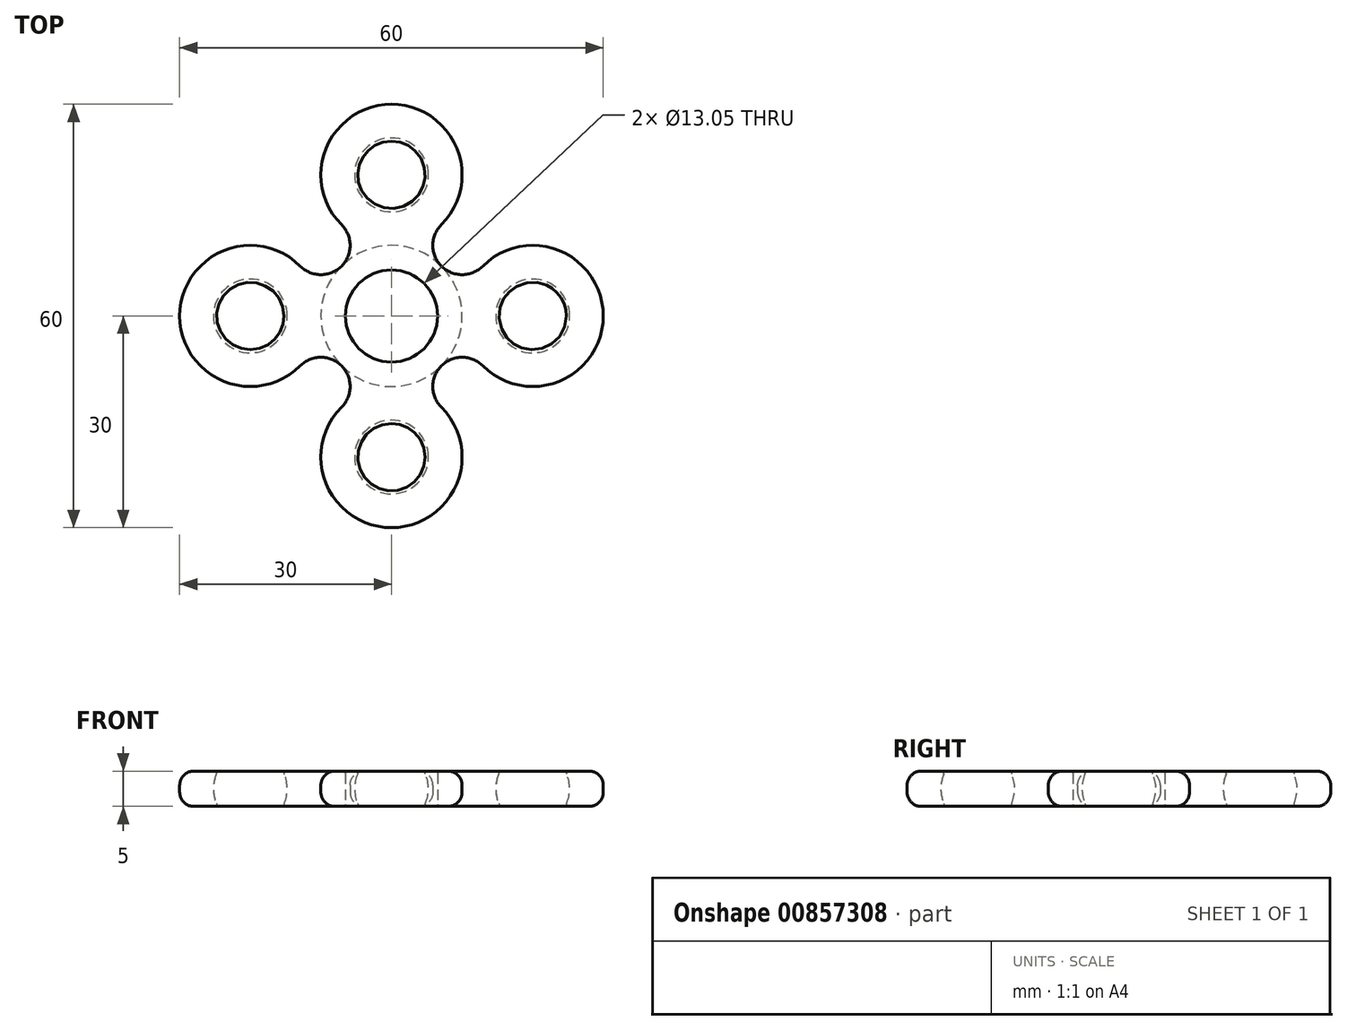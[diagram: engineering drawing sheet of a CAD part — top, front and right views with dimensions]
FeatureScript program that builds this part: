
annotation { "Feature Type Name" : "Feature", "Feature Type Description" : "" }
export const myFeature = defineFeature(function(context is Context, id is Id, definition is map)
    precondition{}
    {
        {
            var Q0;
            Q0=qCreatedBy(makeId("Top.planeOp"),FACE);
            var sketch = newSketch(context, id + "F0", { "sketchPlane" : qUnion([Q0])});
            skArc(sketch, "E0", {"start": v(-7.07, -7.07) * mm, "mid": v(0, -10) * mm, "end": v(7.07, -7.07) * mm});
            skArc(sketch, "E1", {"start": v(12.93, -7.07) * mm, "mid": v(30, 0) * mm, "end": v(12.93, 7.07) * mm});
            skArc(sketch, "E2", {"start": v(-12.93, 7.07) * mm, "mid": v(-30, 0) * mm, "end": v(-12.93, -7.07) * mm});
            skArc(sketch, "E3", {"start": v(7.07, 7.07) * mm, "mid": v(10, 5.86) * mm, "end": v(12.93, 7.07) * mm});
            skArc(sketch, "E4", {"start": v(-12.93, 7.07) * mm, "mid": v(-10, 5.86) * mm, "end": v(-7.07, 7.07) * mm});
            skArc(sketch, "E5.trimOffspring", {"start": v(7.07, 7.07) * mm, "mid": v(0, 10) * mm, "end": v(-7.07, 7.07) * mm});
            skArc(sketch, "E6", {"start": v(-7.07, -7.07) * mm, "mid": v(-10, -5.86) * mm, "end": v(-12.93, -7.07) * mm});
            skArc(sketch, "E7", {"start": v(12.93, -7.07) * mm, "mid": v(10, -5.86) * mm, "end": v(7.07, -7.07) * mm});
            skCircle(sketch, "E8", {"center": v(0, 0) * mm, "radius": 6.53 * mm});
            skSolve(sketch);
        }
        {
            var Q0;
            Q0=makeQuery(id+"F0.imprint","IMPRINT",FACE,{"disambiguationData":[TD([[makeQuery(id+"F0.imprint","IMPRINT",EDGE,{"derivedFrom":sQuery(id+"F0.wireOp",EDGE,"E0")}),1.0]])]});
            extrude(context, id + "F1", {"entities" : qUnion([Q0]), "depth" : 2.5 * mm, "offsetDistance" : 25 * mm});
        }
        {
            var Q0;
            Q0=makeQuery(id+"F1.opExtrude","CAP_FACE",FACE,{"disambiguationData":[OSD([sQuery(id+"F0.wireOp",EDGE,"E0"),sQuery(id+"F0.wireOp",EDGE,"E1"),sQuery(id+"F0.wireOp",EDGE,"E2"),sQuery(id+"F0.wireOp",EDGE,"E3"),sQuery(id+"F0.wireOp",EDGE,"E4"),sQuery(id+"F0.wireOp",EDGE,"E5.trimOffspring"),sQuery(id+"F0.wireOp",EDGE,"E6"),sQuery(id+"F0.wireOp",EDGE,"E7"),sQuery(id+"F0.wireOp",EDGE,"E8")])],"isStart":true});
            extrude(context, id + "F2", {"entities" : qUnion([Q0]), "operationType" : NewBodyOperationType.ADD, "depth" : 2.5 * mm, "offsetDistance" : 25 * mm});
        }
        {
            var Q0;
            Q0=qCreatedBy(makeId("Front.planeOp"),FACE);
            var sketch = newSketch(context, id + "F3", { "sketchPlane" : qUnion([Q0])});
            skArc(sketch, "E9", {"start": v(-20, 5.23) * mm, "mid": v(-25.23, 0) * mm, "end": v(-20, -5.23) * mm});
            skLineSegment(sketch, "E10", {"start": v(-20, 5.23) * mm, "end": v(-20, -5.23) * mm});
            skSolve(sketch);
        }
        {
            var Q0;
            Q0=qSketchRegion(id+"F3",true);
            var Q1;
            Q1=sQuery(id+"F3.wireOp",EDGE,"E10");
            revolve(context, id + "F4", {"operationType" : NewBodyOperationType.REMOVE, "entities" : qUnion([Q0]), "axis" : qUnion([Q1]), "revolveType" : RevolveType.FULL, "oppositeDirection" : true, "surfaceOperationType" : NewSurfaceOperationType.NEW});
        }
        {
            var Q0;
            Q0=qCreatedBy(makeId("Front.planeOp"),FACE);
            var sketch = newSketch(context, id + "F5", { "sketchPlane" : qUnion([Q0])});
            skArc(sketch, "E11", {"start": v(20, -5.23) * mm, "mid": v(25.23, 0) * mm, "end": v(20, 5.23) * mm});
            skLineSegment(sketch, "E12", {"start": v(20, 5.23) * mm, "end": v(20, -5.23) * mm});
            skPoint(sketch, "E13.orphan", {"position": v(20, 9.13) * mm});
            skSolve(sketch);
        }
        {
            var Q0;
            Q0=makeQuery(id+"F5.imprint","IMPRINT",FACE,{"disambiguationData":[TD([[makeQuery(id+"F5.imprint","IMPRINT",EDGE,{"derivedFrom":sQuery(id+"F5.wireOp",EDGE,"E11")}),1.0]])]});
            var Q1;
            Q1=sQuery(id+"F5.wireOp",EDGE,"E12");
            revolve(context, id + "F6", {"operationType" : NewBodyOperationType.REMOVE, "entities" : qUnion([Q0]), "axis" : qUnion([Q1]), "revolveType" : RevolveType.FULL, "oppositeDirection" : true});
        }
        {
            var Q0;
            Q0=makeQuery(id+"F2.opExtrude","CAP_EDGE",EDGE,{"disambiguationData":[OSD([sQuery(id+"F0.wireOp",EDGE,"E6")])],"isStart":false});
            var Q1;
            Q1=makeQuery(id+"F1.opExtrude","CAP_EDGE",EDGE,{"disambiguationData":[OSD([sQuery(id+"F0.wireOp",EDGE,"E0")])],"isStart":false});
            fillet(context, id + "F7", {"entities" : qUnion([Q0, Q1]), "radius" : 2 * mm, "tangentPropagation" : true, "allowEdgeOverflow" : false});
        }
        {
            var Q0;
            Q0=makeQuery(id+"F6.boolean.opBoolean","COPY",FACE,{"derivedFrom":makeQuery(id+"F6.opRevolve","SWEPT_FACE",FACE,{"disambiguationData":[OSD([sQuery(id+"F5.wireOp",EDGE,"E11")])]})});
            var Q1;
            {var subQ0=sQuery(id+"F0.wireOp",EDGE,"E8");Q1=makeQuery(id+"F2.boolean.opBoolean","MERGE",FACE,{"derivedFrom":[makeQuery(id+"F1.opExtrude","SWEPT_FACE",FACE,{"disambiguationData":[OSD([subQ0])]}),makeQuery(id+"F2.opExtrude","SWEPT_FACE",FACE,{"disambiguationData":[OSD([subQ0])]})]});}
            var Q2;
            Q2=makeQuery(id+"F4.boolean.opBoolean","COPY",FACE,{"derivedFrom":makeQuery(id+"F4.opRevolve","SWEPT_FACE",FACE,{"disambiguationData":[OSD([sQuery(id+"F3.wireOp",EDGE,"E9")])]})});
            fillet(context, id + "F8", {"entities" : qUnion([Q0, Q1, Q2]), "radius" : .3 * mm, "tangentPropagation" : true, "allowEdgeOverflow" : false});
        }
        {
            var Q0;
            Q0=makeQuery(id+"F1.opExtrude","SWEPT_BODY",BODY,{"disambiguationData":[OSD([sQuery(id+"F0.wireOp",EDGE,"E0"),sQuery(id+"F0.wireOp",EDGE,"E1"),sQuery(id+"F0.wireOp",EDGE,"E2"),sQuery(id+"F0.wireOp",EDGE,"E3"),sQuery(id+"F0.wireOp",EDGE,"E4"),sQuery(id+"F0.wireOp",EDGE,"E5.trimOffspring"),sQuery(id+"F0.wireOp",EDGE,"E6"),sQuery(id+"F0.wireOp",EDGE,"E7"),sQuery(id+"F0.wireOp",EDGE,"E8")])]});
            var Q1;
            {var subQ0=sQuery(id+"F0.wireOp",EDGE,"E8");Q1=makeQuery(id+"F8.opFillet","BLEND_EDGE",EDGE,{"blendedFrom":[makeQuery(id+"F1.opExtrude","CAP_EDGE",EDGE,{"disambiguationData":[OSD([subQ0])],"isStart":false}),makeQuery(id+"F2.boolean.opBoolean","MERGE",FACE,{"derivedFrom":[makeQuery(id+"F1.opExtrude","SWEPT_FACE",FACE,{"disambiguationData":[OSD([subQ0])]}),makeQuery(id+"F2.opExtrude","SWEPT_FACE",FACE,{"disambiguationData":[OSD([subQ0])]})]})],"blendedInto":[makeQuery(id+"F2.boolean.opBoolean","MERGE",FACE,{"derivedFrom":[makeQuery(id+"F1.opExtrude","SWEPT_FACE",FACE,{"disambiguationData":[OSD([subQ0])]}),makeQuery(id+"F2.opExtrude","SWEPT_FACE",FACE,{"disambiguationData":[OSD([subQ0])]})]})]});}
            circularPattern(context, id + "F9", {"entities" : qUnion([Q0]), "axis" : qUnion([Q1]), "angle" : 90 * degree, "instanceCount" : 2, "equalSpace" : true});
        }
    });
